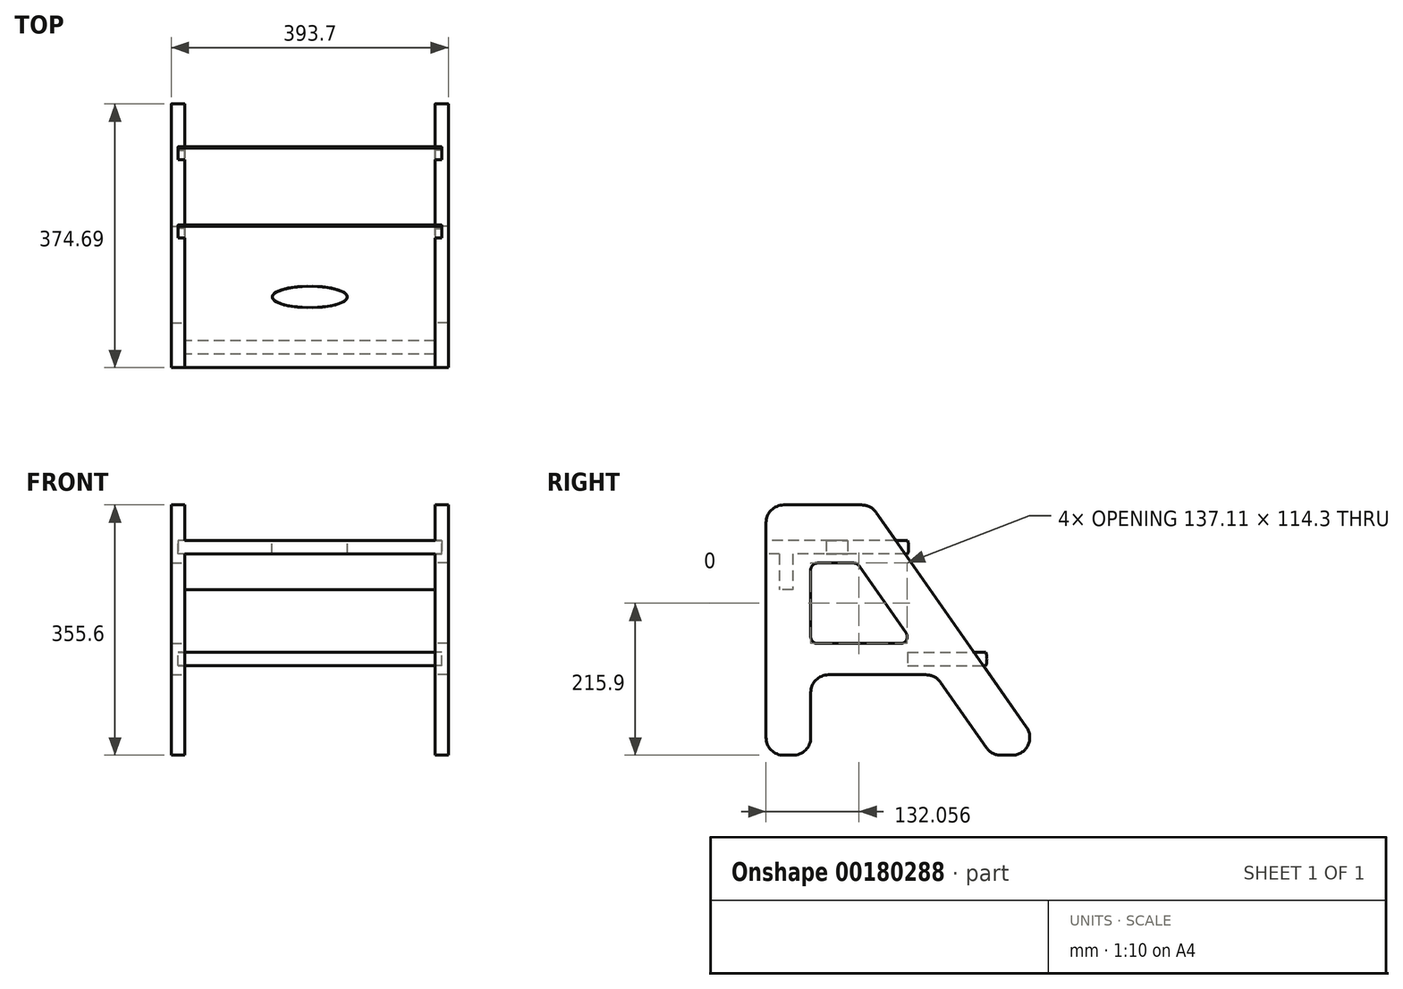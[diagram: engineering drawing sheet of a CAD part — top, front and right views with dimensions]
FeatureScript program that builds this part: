
annotation { "Feature Type Name" : "Feature", "Feature Type Description" : "" }
export const myFeature = defineFeature(function(context is Context, id is Id, definition is map)
    precondition{}
    {
        {
            var Q0;
            Q0=qCreatedBy(makeId("Right.planeOp"),FACE);
            cPlane(context, id + "F0", {"entities" : qUnion([Q0]), "cplaneType" : CPlaneType.OFFSET, "offset" : 177.8 * mm, "oppositeDirection" : true, "width" : 152.4 * mm, "height" : 152.4 * mm});
        }
        {
            var Q0;
            Q0=qCreatedBy(id+"F0.planeOp",FACE);
            var sketch = newSketch(context, id + "F1", { "sketchPlane" : qUnion([Q0])});
            skLineSegment(sketch, "E0", {"start": v(-48.8, 0) * mm, "end": v(-64.3, 0) * mm});
            skLineSegment(sketch, "E1", {"start": v(-372.68, 0) * mm, "end": v(-359.98, 0) * mm});
            skLineSegment(sketch, "E2", {"start": v(-398.08, 25.4) * mm, "end": v(-398.08, 330.2) * mm});
            skLineSegment(sketch, "E3", {"start": v(-372.68, 355.6) * mm, "end": v(-262.22, 355.6) * mm});
            skLineSegment(sketch, "E4", {"start": v(-241.4, 344.77) * mm, "end": v(-27.99, 39.97) * mm});
            skLineSegment(sketch, "E5", {"start": v(-85.1, 10.83) * mm, "end": v(-149.97, 103.47) * mm});
            skLineSegment(sketch, "E6", {"start": v(-170.78, 114.3) * mm, "end": v(-309.18, 114.3) * mm});
            skLineSegment(sketch, "E7", {"start": v(-334.58, 88.9) * mm, "end": v(-334.58, 25.4) * mm});
            skPoint(sketch, "E8.visualSharp", {"position": v(-398.08, 0) * mm});
            skArc(sketch, "E8.filletArc", {"start": v(-398.08, 25.4) * mm, "mid": v(-390.64, 7.44) * mm, "end": v(-372.68, 0) * mm});
            skPoint(sketch, "E9.visualSharp", {"position": v(-334.58, 0) * mm});
            skArc(sketch, "E9.filletArc", {"start": v(-359.98, 0) * mm, "mid": v(-342.02, 7.44) * mm, "end": v(-334.58, 25.4) * mm});
            skPoint(sketch, "E10.visualSharp", {"position": v(-77.52, 0) * mm});
            skArc(sketch, "E10.filletArc", {"start": v(-85.1, 10.83) * mm, "mid": v(-76.03, 2.87) * mm, "end": v(-64.3, 0) * mm});
            skPoint(sketch, "E11.visualSharp", {"position": v(0, 0) * mm});
            skArc(sketch, "E11.filletArc", {"start": v(-48.8, 0) * mm, "mid": v(-26.26, 13.67) * mm, "end": v(-27.99, 39.97) * mm});
            skPoint(sketch, "E12.visualSharp", {"position": v(-398.08, 355.6) * mm});
            skArc(sketch, "E12.filletArc", {"start": v(-372.68, 355.6) * mm, "mid": v(-390.64, 348.16) * mm, "end": v(-398.08, 330.2) * mm});
            skPoint(sketch, "E13.visualSharp", {"position": v(-249, 355.6) * mm});
            skArc(sketch, "E13.filletArc", {"start": v(-241.4, 344.77) * mm, "mid": v(-250.49, 352.73) * mm, "end": v(-262.22, 355.6) * mm});
            skPoint(sketch, "E14.visualSharp", {"position": v(-334.58, 114.3) * mm});
            skArc(sketch, "E14.filletArc", {"start": v(-309.18, 114.3) * mm, "mid": v(-327.14, 106.86) * mm, "end": v(-334.58, 88.9) * mm});
            skPoint(sketch, "E15.visualSharp", {"position": v(-157.55, 114.3) * mm});
            skArc(sketch, "E15.filletArc", {"start": v(-149.97, 103.47) * mm, "mid": v(-159.05, 111.43) * mm, "end": v(-170.78, 114.3) * mm});
            skLineSegment(sketch, "E16", {"start": v(-334.58, 263.53) * mm, "end": v(-334.58, 168.27) * mm});
            skLineSegment(sketch, "E17", {"start": v(-325.05, 158.75) * mm, "end": v(-206.97, 158.75) * mm});
            skLineSegment(sketch, "E18", {"start": v(-199.17, 173.74) * mm, "end": v(-265.87, 268.99) * mm});
            skLineSegment(sketch, "E19", {"start": v(-273.67, 273.05) * mm, "end": v(-325.05, 273.05) * mm});
            skPoint(sketch, "E20.visualSharp", {"position": v(-334.58, 273.05) * mm});
            skArc(sketch, "E20.filletArc", {"start": v(-325.05, 273.05) * mm, "mid": v(-331.79, 270.26) * mm, "end": v(-334.58, 263.53) * mm});
            skPoint(sketch, "E21.visualSharp", {"position": v(-268.71, 273.05) * mm});
            skArc(sketch, "E21.filletArc", {"start": v(-265.87, 268.99) * mm, "mid": v(-269.27, 271.97) * mm, "end": v(-273.67, 273.05) * mm});
            skPoint(sketch, "E22.visualSharp", {"position": v(-334.58, 158.75) * mm});
            skArc(sketch, "E22.filletArc", {"start": v(-334.58, 168.27) * mm, "mid": v(-331.79, 161.54) * mm, "end": v(-325.05, 158.75) * mm});
            skPoint(sketch, "E23.visualSharp", {"position": v(-188.68, 158.75) * mm});
            skArc(sketch, "E23.filletArc", {"start": v(-206.97, 158.75) * mm, "mid": v(-198.53, 163.88) * mm, "end": v(-199.17, 173.74) * mm});
            skSolve(sketch);
        }
        {
            var Q0;
            Q0 = qSketchRegion(id + "F1", true);
            extrude(context, id + "F2", {"entities" : qUnion([Q0]), "oppositeDirection" : true, "depth" : 19.05 * mm});
        }
        {
            var Q0;
            Q0=makeQuery(id+"F2.opExtrude","SWEPT_FACE",FACE,{"disambiguationData":[OSD([sQuery(id+"F1.wireOp",EDGE,"E2")])]});
            var sketch = newSketch(context, id + "F3", { "sketchPlane" : qUnion([Q0])});
            skLineSegment(sketch, "E24.bottom", {"start": v(-177.8, 304.8) * mm, "end": v(-187.33, 304.8) * mm});
            skLineSegment(sketch, "E24.top", {"start": v(-177.8, 285.75) * mm, "end": v(-187.33, 285.75) * mm});
            skLineSegment(sketch, "E24.left", {"start": v(-177.8, 304.8) * mm, "end": v(-177.8, 285.75) * mm});
            skLineSegment(sketch, "E24.right", {"start": v(-187.33, 304.8) * mm, "end": v(-187.33, 285.75) * mm});
            skSolve(sketch);
        }
        {
            var Q0;
            Q0=makeQuery(id+"F3.imprint","IMPRINT",FACE,{"disambiguationData":[TD([[makeQuery(id+"F3.imprint","IMPRINT",EDGE,{"derivedFrom":sQuery(id+"F3.wireOp",EDGE,"E24.bottom")}),1.0]])]});
            extrude(context, id + "F4", {"entities" : qUnion([Q0]), "operationType" : NewBodyOperationType.REMOVE, "oppositeDirection" : true, "depth" : 223.52 * mm});
        }
        {
            var Q0;
            Q0=qCreatedBy(makeId("Front.planeOp"),FACE);
            var sketch = newSketch(context, id + "F5", { "sketchPlane" : qUnion([Q0])});
            skLineSegment(sketch, "E25.bottom", {"start": v(-177.8, 146.05) * mm, "end": v(-187.32, 146.05) * mm});
            skLineSegment(sketch, "E25.top", {"start": v(-177.8, 127) * mm, "end": v(-187.33, 127) * mm});
            skLineSegment(sketch, "E25.left", {"start": v(-177.8, 146.05) * mm, "end": v(-177.8, 127) * mm});
            skLineSegment(sketch, "E25.right", {"start": v(-187.32, 146.05) * mm, "end": v(-187.32, 127) * mm});
            skSolve(sketch);
        }
        {
            var Q0;
            Q0 = qSketchRegion(id + "F5", true);
            extrude(context, id + "F6", {"entities" : qUnion([Q0]), "operationType" : NewBodyOperationType.REMOVE, "depth" : 196.85 * mm});
        }
        {
            var Q0;
            Q0=makeQuery(id+"F6.boolean.opBoolean","COPY",FACE,{"derivedFrom":makeQuery(id+"F6.opExtrude","SWEPT_FACE",FACE,{"disambiguationData":[OSD([sQuery(id+"F5.wireOp",EDGE,"E25.right")])]})});
            var sketch = newSketch(context, id + "F7", { "sketchPlane" : qUnion([Q0])});
            skLineSegment(sketch, "E26.0.1", {"start": v(-102.27, 146.05) * mm, "end": v(-196.85, 146.05) * mm});
            skLineSegment(sketch, "E26.0.2", {"start": v(-196.85, 146.05) * mm, "end": v(-196.85, 127) * mm});
            skLineSegment(sketch, "E26.0.3", {"start": v(-196.85, 127) * mm, "end": v(-88.93, 127) * mm});
            skLineSegment(sketch, "E27", {"start": v(-102.27, 146.05) * mm, "end": v(-88.93, 146.05) * mm});
            skLineSegment(sketch, "E28", {"start": v(-88.93, 127) * mm, "end": v(-85.75, 127) * mm});
            skLineSegment(sketch, "E29", {"start": v(-85.75, 146.05) * mm, "end": v(-88.93, 146.05) * mm});
            skArc(sketch, "E30", {"start": v(-85.75, 127) * mm, "mid": v(-84.29, 136.52) * mm, "end": v(-85.75, 146.05) * mm});
            skLineSegment(sketch, "E31.0.0", {"start": v(-213.42, 304.8) * mm, "end": v(-398.08, 304.8) * mm});
            skLineSegment(sketch, "E31.0.1", {"start": v(-398.08, 304.8) * mm, "end": v(-398.08, 285.75) * mm});
            skLineSegment(sketch, "E31.0.2", {"start": v(-398.08, 285.75) * mm, "end": v(-200.08, 285.75) * mm});
            skLineSegment(sketch, "E31.0.3", {"start": v(-200.08, 285.75) * mm, "end": v(-213.42, 304.8) * mm});
            skLineSegment(sketch, "E32", {"start": v(-200.08, 285.75) * mm, "end": v(-196.9, 285.75) * mm});
            skLineSegment(sketch, "E33", {"start": v(-196.9, 304.8) * mm, "end": v(-213.42, 304.8) * mm});
            skArc(sketch, "E34", {"start": v(-196.9, 285.75) * mm, "mid": v(-195.45, 295.27) * mm, "end": v(-196.9, 304.8) * mm});
            skSolve(sketch);
        }
        {
            var Q0;
            Q0 = qSketchRegion(id + "F7", true);
            var Q1;
            Q1=qCreatedBy(makeId("Right.planeOp"),FACE);
            extrude(context, id + "F8", {"entities" : qUnion([Q0]), "operationType" : NewBodyOperationType.ADD, "endBound" : BoundingType.UP_TO_SURFACE, "endBoundEntityFace" : qUnion([Q1]), "depth" : 25.4 * mm});
        }
        {
            var Q0;
            Q0=makeQuery(id+"F8.opExtrude","SWEPT_FACE",FACE,{"disambiguationData":[OSD([sQuery(id+"F7.wireOp",EDGE,"E31.0.0"),sQuery(id+"F7.wireOp",EDGE,"E33")])]});
            var sketch = newSketch(context, id + "F9", { "sketchPlane" : qUnion([Q0])});
            skEllipse(sketch, "E35", {"center": v(0, -297.5) * mm, "majorRadius": 53.58 * mm, "minorRadius": 15.2 * mm, "majorAxis": v(-1, 0)});
            skSolve(sketch);
        }
        {
            var Q0;
            Q0 = qSketchRegion(id + "F9", true);
            extrude(context, id + "F10", {"entities" : qUnion([Q0]), "operationType" : NewBodyOperationType.REMOVE, "oppositeDirection" : true, "depth" : 25.4 * mm});
        }
        {
            var Q0;
            Q0=makeQuery(id+"F2.opExtrude","SWEPT_BODY",BODY,{"disambiguationData":[OSD([sQuery(id+"F1.wireOp",EDGE,"E0"),sQuery(id+"F1.wireOp",EDGE,"E1"),sQuery(id+"F1.wireOp",EDGE,"E2"),sQuery(id+"F1.wireOp",EDGE,"E3"),sQuery(id+"F1.wireOp",EDGE,"E4"),sQuery(id+"F1.wireOp",EDGE,"E5"),sQuery(id+"F1.wireOp",EDGE,"E6"),sQuery(id+"F1.wireOp",EDGE,"E7"),sQuery(id+"F1.wireOp",EDGE,"E8.filletArc"),sQuery(id+"F1.wireOp",EDGE,"E9.filletArc"),sQuery(id+"F1.wireOp",EDGE,"E10.filletArc"),sQuery(id+"F1.wireOp",EDGE,"E11.filletArc"),sQuery(id+"F1.wireOp",EDGE,"E12.filletArc"),sQuery(id+"F1.wireOp",EDGE,"E13.filletArc"),sQuery(id+"F1.wireOp",EDGE,"E14.filletArc"),sQuery(id+"F1.wireOp",EDGE,"E15.filletArc")])]});
            var Q1;
            Q1=qCreatedBy(makeId("Right.planeOp"),FACE);
            mirror(context, id + "F11", {"operationType" : NewBodyOperationType.ADD, "entities" : qUnion([Q0]), "mirrorPlane" : qUnion([Q1])});
        }
        {
            var Q0;
            {var subQ0=sQuery(id+"F1.wireOp",EDGE,"E10.filletArc");var subQ1=sQuery(id+"F1.wireOp",EDGE,"E9.filletArc");var subQ2=sQuery(id+"F1.wireOp",EDGE,"E16");var subQ3=sQuery(id+"F1.wireOp",EDGE,"E7");var subQ4=sQuery(id+"F1.wireOp",EDGE,"E14.filletArc");var subQ5=sQuery(id+"F1.wireOp",EDGE,"E6");var subQ6=sQuery(id+"F1.wireOp",EDGE,"E5");var subQ7=sQuery(id+"F1.wireOp",EDGE,"E0");var subQ8=sQuery(id+"F1.wireOp",EDGE,"E20.filletArc");var subQ9=sQuery(id+"F1.wireOp",EDGE,"E8.filletArc");var subQ10=sQuery(id+"F1.wireOp",EDGE,"E1");var subQ11=sQuery(id+"F1.wireOp",EDGE,"E23.filletArc");var subQ12=sQuery(id+"F1.wireOp",EDGE,"E2");var subQ13=sQuery(id+"F1.wireOp",EDGE,"E4");var subQ14=sQuery(id+"F1.wireOp",EDGE,"E11.filletArc");var subQ15=sQuery(id+"F1.wireOp",EDGE,"E18");var subQ16=sQuery(id+"F1.wireOp",EDGE,"E15.filletArc");var subQ17=sQuery(id+"F1.wireOp",EDGE,"E17");var subQ18=sQuery(id+"F1.wireOp",EDGE,"E19");var subQ19=sQuery(id+"F1.wireOp",EDGE,"E21.filletArc");var subQ20=sQuery(id+"F1.wireOp",EDGE,"E22.filletArc");Q0=makeQuery(id+"F4.boolean.opBoolean","SPLIT",FACE,{"disambiguationData":[TD([makeQuery(id+"F2.opExtrude","SWEPT_FACE",FACE,{"disambiguationData":[OSD([subQ7])]})])],"derivedFrom":makeQuery(id+"F2.opExtrude","CAP_FACE",FACE,{"disambiguationData":[OSD([subQ7,subQ10,subQ12,sQuery(id+"F1.wireOp",EDGE,"E3"),subQ13,subQ6,subQ5,subQ3,subQ9,subQ1,subQ0,subQ14,sQuery(id+"F1.wireOp",EDGE,"E12.filletArc"),sQuery(id+"F1.wireOp",EDGE,"E13.filletArc"),subQ4,subQ16,subQ2,subQ17,subQ15,subQ18,subQ8,subQ19,subQ20,subQ11])],"isStart":true})});}
            var sketch = newSketch(context, id + "F12", { "sketchPlane" : qUnion([Q0])});
            skLineSegment(sketch, "E36.bottom", {"start": v(-359.98, 285.75) * mm, "end": v(-379.03, 285.75) * mm});
            skLineSegment(sketch, "E36.top", {"start": v(-359.98, 234.95) * mm, "end": v(-379.03, 234.95) * mm});
            skLineSegment(sketch, "E36.left", {"start": v(-359.98, 285.75) * mm, "end": v(-359.98, 234.95) * mm});
            skLineSegment(sketch, "E36.right", {"start": v(-379.03, 285.75) * mm, "end": v(-379.03, 234.95) * mm});
            skSolve(sketch);
        }
        {
            var Q0;
            Q0=makeQuery(id+"F12.imprint","IMPRINT",FACE,{"disambiguationData":[TD([[makeQuery(id+"F12.imprint","IMPRINT",EDGE,{"derivedFrom":sQuery(id+"F12.wireOp",EDGE,"E36.bottom")}),1.0]])]});
            var Q1;
            {var subQ0=sQuery(id+"F1.wireOp",EDGE,"E10.filletArc");var subQ1=sQuery(id+"F1.wireOp",EDGE,"E9.filletArc");var subQ2=sQuery(id+"F1.wireOp",EDGE,"E16");var subQ3=sQuery(id+"F1.wireOp",EDGE,"E7");var subQ4=sQuery(id+"F1.wireOp",EDGE,"E14.filletArc");var subQ5=sQuery(id+"F1.wireOp",EDGE,"E6");var subQ6=sQuery(id+"F1.wireOp",EDGE,"E5");var subQ7=sQuery(id+"F1.wireOp",EDGE,"E0");var subQ8=sQuery(id+"F1.wireOp",EDGE,"E20.filletArc");var subQ9=sQuery(id+"F1.wireOp",EDGE,"E8.filletArc");var subQ10=sQuery(id+"F1.wireOp",EDGE,"E1");var subQ11=sQuery(id+"F1.wireOp",EDGE,"E23.filletArc");var subQ12=sQuery(id+"F1.wireOp",EDGE,"E2");var subQ13=sQuery(id+"F1.wireOp",EDGE,"E4");var subQ14=sQuery(id+"F1.wireOp",EDGE,"E11.filletArc");var subQ15=sQuery(id+"F1.wireOp",EDGE,"E18");var subQ16=sQuery(id+"F1.wireOp",EDGE,"E15.filletArc");var subQ17=sQuery(id+"F1.wireOp",EDGE,"E17");var subQ18=sQuery(id+"F1.wireOp",EDGE,"E19");var subQ19=sQuery(id+"F1.wireOp",EDGE,"E21.filletArc");var subQ20=sQuery(id+"F1.wireOp",EDGE,"E22.filletArc");Q1=makeQuery(id+"F11.opPattern","COPY",FACE,{"derivedFrom":makeQuery(id+"F4.boolean.opBoolean","SPLIT",FACE,{"disambiguationData":[TD([makeQuery(id+"F2.opExtrude","SWEPT_FACE",FACE,{"disambiguationData":[OSD([subQ7])]})])],"derivedFrom":makeQuery(id+"F2.opExtrude","CAP_FACE",FACE,{"disambiguationData":[OSD([subQ7,subQ10,subQ12,sQuery(id+"F1.wireOp",EDGE,"E3"),subQ13,subQ6,subQ5,subQ3,subQ9,subQ1,subQ0,subQ14,sQuery(id+"F1.wireOp",EDGE,"E12.filletArc"),sQuery(id+"F1.wireOp",EDGE,"E13.filletArc"),subQ4,subQ16,subQ2,subQ17,subQ15,subQ18,subQ8,subQ19,subQ20,subQ11])],"isStart":true})}),"instanceName":"1"});}
            extrude(context, id + "F13", {"entities" : qUnion([Q0]), "operationType" : NewBodyOperationType.ADD, "endBound" : BoundingType.UP_TO_SURFACE, "endBoundEntityFace" : qUnion([Q1]), "depth" : 25.4 * mm});
        }
        {
            var Q0;
            Q0=makeQuery(id+"F2.opExtrude","SWEPT_BODY",BODY,{"disambiguationData":[OSD([sQuery(id+"F1.wireOp",EDGE,"E0"),sQuery(id+"F1.wireOp",EDGE,"E1"),sQuery(id+"F1.wireOp",EDGE,"E2"),sQuery(id+"F1.wireOp",EDGE,"E3"),sQuery(id+"F1.wireOp",EDGE,"E4"),sQuery(id+"F1.wireOp",EDGE,"E5"),sQuery(id+"F1.wireOp",EDGE,"E6"),sQuery(id+"F1.wireOp",EDGE,"E7"),sQuery(id+"F1.wireOp",EDGE,"E8.filletArc"),sQuery(id+"F1.wireOp",EDGE,"E9.filletArc"),sQuery(id+"F1.wireOp",EDGE,"E10.filletArc"),sQuery(id+"F1.wireOp",EDGE,"E11.filletArc"),sQuery(id+"F1.wireOp",EDGE,"E12.filletArc"),sQuery(id+"F1.wireOp",EDGE,"E13.filletArc"),sQuery(id+"F1.wireOp",EDGE,"E14.filletArc"),sQuery(id+"F1.wireOp",EDGE,"E15.filletArc")])]});
            var Q1;
            Q1=qCreatedBy(makeId("Right.planeOp"),FACE);
            mirror(context, id + "F14", {"entities" : qUnion([Q0]), "mirrorPlane" : qUnion([Q1])});
        }
    });
